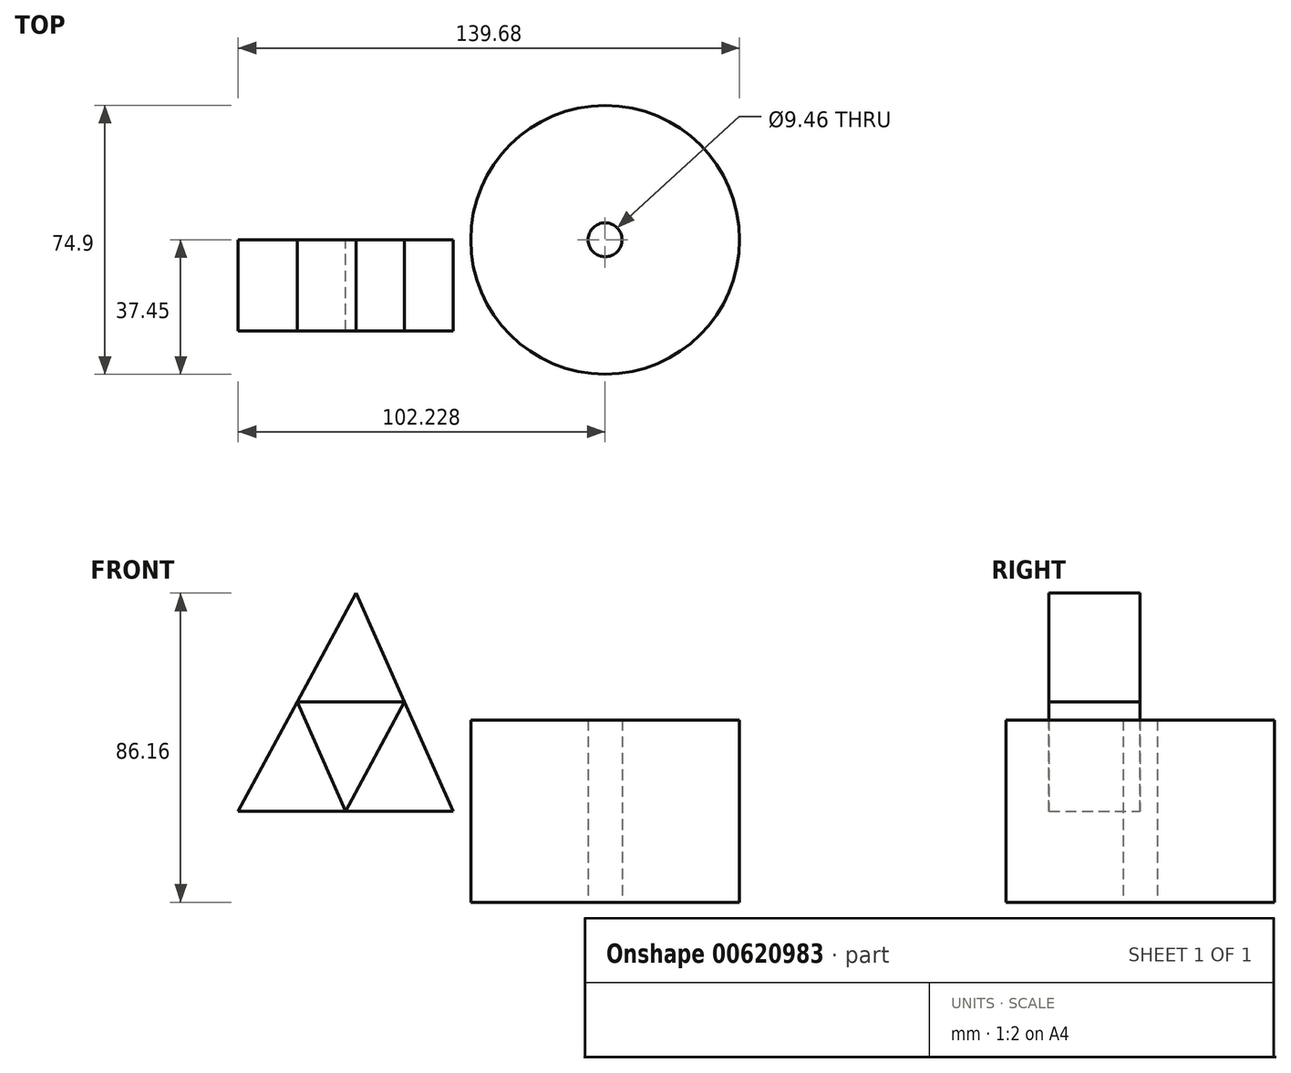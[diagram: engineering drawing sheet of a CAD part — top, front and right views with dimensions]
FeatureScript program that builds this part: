
annotation { "Feature Type Name" : "Feature", "Feature Type Description" : "" }
export const myFeature = defineFeature(function(context is Context, id is Id, definition is map)
    precondition{}
    {
        {
            var Q0;
            Q0=qCreatedBy(makeId("Front.planeOp"),FACE);
            var sketch = newSketch(context, id + "F0", { "sketchPlane" : qUnion([Q0])});
            skLineSegment(sketch, "E0", {"start": v(-64.68, 0) * mm, "end": v(-31.9, 60.76) * mm});
            skLineSegment(sketch, "E1", {"start": v(-31.9, 60.76) * mm, "end": v(-4.76, 0) * mm});
            skLineSegment(sketch, "E2", {"start": v(-4.76, 0) * mm, "end": v(-64.68, 0) * mm});
            skLineSegment(sketch, "E3", {"start": v(-34.72, 0) * mm, "end": v(-48.3, 30.38) * mm});
            skLineSegment(sketch, "E4", {"start": v(-48.3, 30.38) * mm, "end": v(-18.33, 30.38) * mm});
            skLineSegment(sketch, "E5", {"start": v(-18.33, 30.38) * mm, "end": v(-34.72, 0) * mm});
            skSolve(sketch);
        }
        {
            var Q0;
            {var subQ3=sQuery(id+"F0.wireOp",EDGE,"E4");Q0=makeQuery(id+"F0.imprint","IMPRINT",FACE,{"disambiguationData":[TD([[makeQuery(id+"F0.imprint","IMPRINT",EDGE,{"derivedFrom":subQ3}),1.0]])]});}
            var Q1;
            {var subQ3=sQuery(id+"F0.wireOp",EDGE,"E3");Q1=makeQuery(id+"F0.imprint","IMPRINT",FACE,{"disambiguationData":[TD([[makeQuery(id+"F0.imprint","IMPRINT",EDGE,{"derivedFrom":subQ3}),1.0]])]});}
            var Q2;
            {var subQ3=sQuery(id+"F0.wireOp",EDGE,"E5");Q2=makeQuery(id+"F0.imprint","IMPRINT",FACE,{"disambiguationData":[TD([[makeQuery(id+"F0.imprint","IMPRINT",EDGE,{"derivedFrom":subQ3}),1.0]])]});}
            extrude(context, id + "F1", {"entities" : qUnion([Q0, Q1, Q2]), "depth" : 25.4 * mm, "offsetDistance" : 25.4 * mm});
        }
        {
            var Q0;
            Q0=qCreatedBy(makeId("Top.planeOp"),FACE);
            var sketch = newSketch(context, id + "F2", { "sketchPlane" : qUnion([Q0])});
            skCircle(sketch, "E6", {"center": v(37.55, 0) * mm, "radius": 37.45 * mm});
            skCircle(sketch, "E7", {"center": v(37.55, 0) * mm, "radius": 4.73 * mm});
            skLineSegment(sketch, "E8", {"start": v(37.55, -4.73) * mm, "end": v(0, 0) * mm});
            skLineSegment(sketch, "E9", {"start": v(36.75, 4.66) * mm, "end": v(-5.6, 11.22) * mm});
            skLineSegment(sketch, "E10", {"start": v(37.55, -4.73) * mm, "end": v(73.8, -9.37) * mm});
            skLineSegment(sketch, "E11", {"start": v(36.75, 4.66) * mm, "end": v(75, 0) * mm});
            skSolve(sketch);
        }
        {
            var Q0;
            Q0 = qSketchRegion(id + "F2", true);
            extrude(context, id + "F3", {"entities" : qUnion([Q0]), "depth" : 25.4 * mm, "offsetDistance" : 25.4 * mm});
        }
        {
            var Q0;
            Q0=makeQuery(id+"F3.opExtrude","CAP_FACE",FACE,{"disambiguationData":[OSD([sQuery(id+"F2.wireOp",EDGE,"E6"),sQuery(id+"F2.wireOp",EDGE,"E7")])],"isStart":true});
            extrude(context, id + "F4", {"entities" : qUnion([Q0]), "operationType" : NewBodyOperationType.ADD, "depth" : 25.4 * mm, "offsetDistance" : 25.4 * mm});
        }
    });
